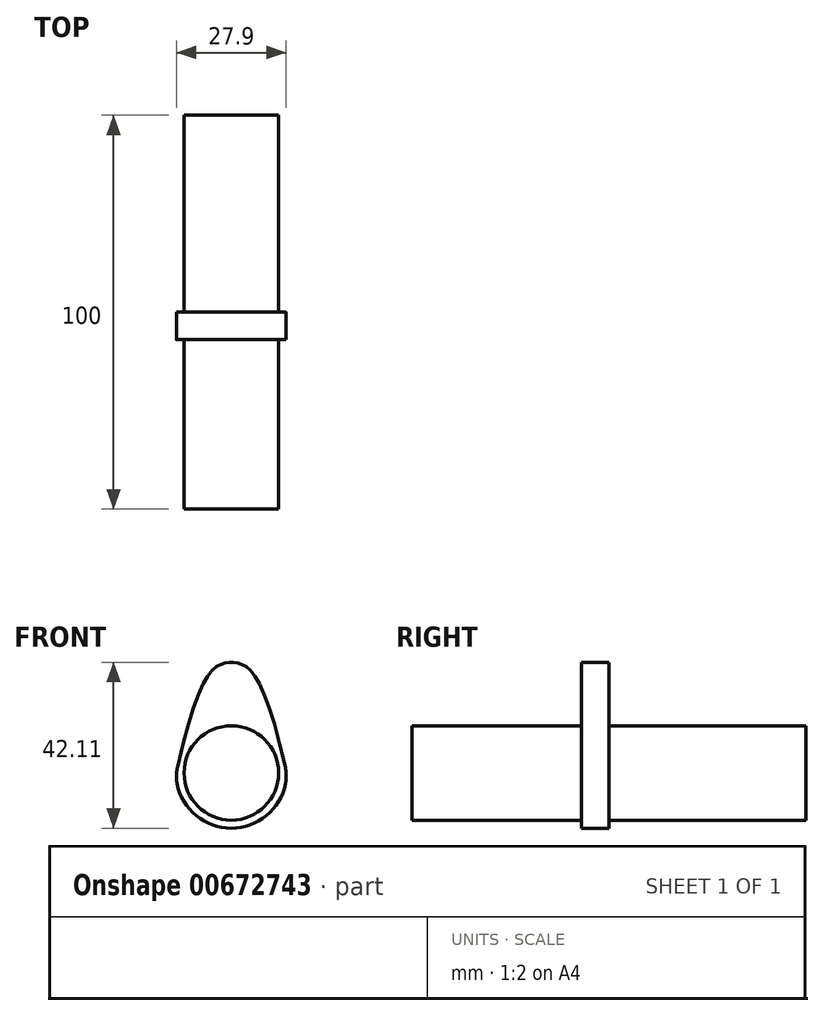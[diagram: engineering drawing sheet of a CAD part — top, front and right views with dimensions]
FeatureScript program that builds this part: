
annotation { "Feature Type Name" : "Feature", "Feature Type Description" : "" }
export const myFeature = defineFeature(function(context is Context, id is Id, definition is map)
    precondition{}
    {
        {
            var Q0;
            Q0=qCreatedBy(makeId("Front.planeOp"),FACE);
            var sketch = newSketch(context, id + "F0", { "sketchPlane" : qUnion([Q0])});
            skCircle(sketch, "E0", {"center": v(0, 0) * mm, "radius": 12 * mm});
            skArc(sketch, "E1", {"start": v(-13.77, -2.67) * mm, "mid": v(0, -14.03) * mm, "end": v(13.77, -2.67) * mm});
            skPoint(sketch, "E2", {"position": v(0, 28.08) * mm});
            skFitSpline(sketch, "E3", {"points": [v(-14.03, 0) * mm, v(0, 28.08) * mm, v(14.03, 0) * mm], "startDerivative": vector(34.65, 158.07) * mm, "endDerivative": vector(34.65, -158.07) * mm});
            skLineSegment(sketch, "E4", {"start": v(-8.25, 26.35) * mm, "end": v(8.25, 26.35) * mm, "construction": true});
            skPoint(sketch, "E5", {"position": v(0, 26.35) * mm});
            skArc(sketch, "E6.filletArc", {"start": v(-13.7, 1.43) * mm, "mid": v(-13.95, -0.62) * mm, "end": v(-13.77, -2.67) * mm});
            skPoint(sketch, "E7.visualSharp", {"position": v(14.02, 0) * mm});
            skArc(sketch, "E7.filletArc", {"start": v(13.77, -2.67) * mm, "mid": v(13.95, -0.62) * mm, "end": v(13.7, 1.43) * mm});
            skSolve(sketch);
        }
        {
            var Q0;
            Q0=makeQuery(id+"F0.imprint","IMPRINT",FACE,{"disambiguationData":[TD([[makeQuery(id+"F0.imprint","IMPRINT",EDGE,{"derivedFrom":sQuery(id+"F0.wireOp",EDGE,"E0")}),1.0]])]});
            extrude(context, id + "F1", {"entities" : qUnion([Q0]), "depth" : 50 * mm, "offsetDistance" : 25 * mm, "hasSecondDirection" : true, "secondDirectionOppositeDirection" : true, "secondDirectionDepth" : 50 * mm});
        }
        {
            var Q0;
            Q0=makeQuery(id+"F0.imprint","IMPRINT",FACE,{"disambiguationData":[TD([[makeQuery(id+"F0.imprint","IMPRINT",EDGE,{"derivedFrom":sQuery(id+"F0.wireOp",EDGE,"E0")}),-1.0]])]});
            extrude(context, id + "F2", {"entities" : qUnion([Q0]), "operationType" : NewBodyOperationType.ADD, "depth" : 7 * mm, "offsetDistance" : 25 * mm});
        }
    });
